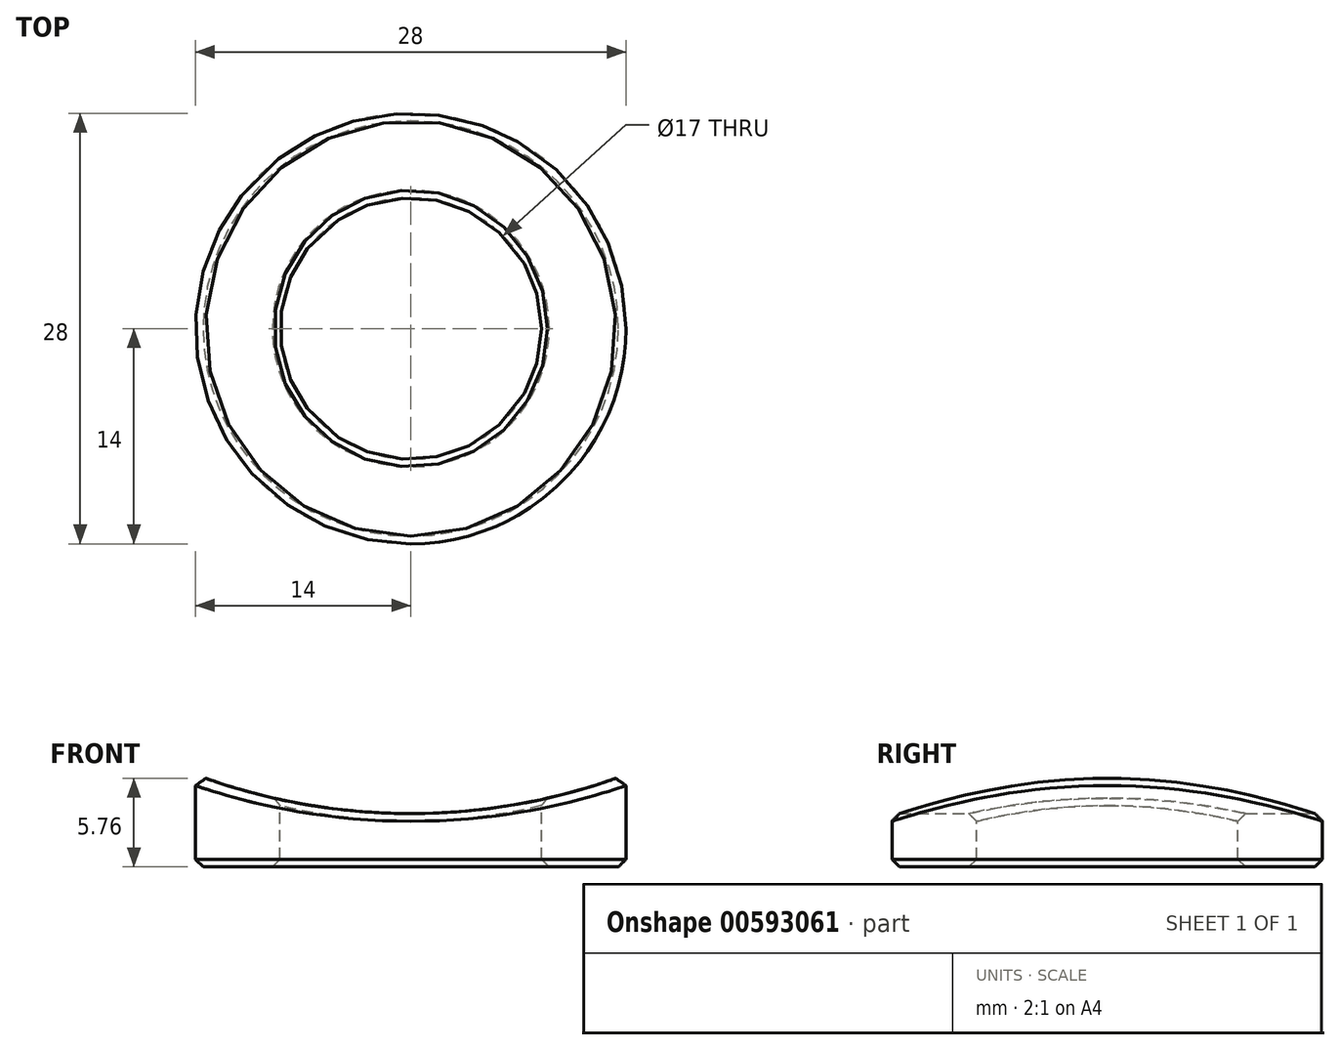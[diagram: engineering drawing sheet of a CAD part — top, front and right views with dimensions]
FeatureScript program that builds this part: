
annotation { "Feature Type Name" : "Feature", "Feature Type Description" : "" }
export const myFeature = defineFeature(function(context is Context, id is Id, definition is map)
    precondition{}
    {
        {
            var Q0;
            Q0=qCreatedBy(makeId("Front.planeOp"),FACE);
            var sketch = newSketch(context, id + "F0", { "sketchPlane" : qUnion([Q0])});
            skArc(sketch, "E0", {"start": v(-14, 6) * mm, "mid": v(0, 3.47) * mm, "end": v(14, 6) * mm});
            skLineSegment(sketch, "E1", {"start": v(-14, 0) * mm, "end": v(14, 0) * mm});
            skLineSegment(sketch, "E2", {"start": v(14, 0) * mm, "end": v(14, 6) * mm});
            skLineSegment(sketch, "E3", {"start": v(-14, 0) * mm, "end": v(-14, 6) * mm});
            skSolve(sketch);
        }
        {
            var Q0;
            Q0=makeQuery(id+"F0.imprint","IMPRINT",FACE,{"disambiguationData":[TD([[makeQuery(id+"F0.imprint","IMPRINT",EDGE,{"derivedFrom":sQuery(id+"F0.wireOp",EDGE,"E0")}),-1.0]])]});
            extrude(context, id + "F1", {"entities" : qUnion([Q0]), "endBound" : BoundingType.SYMMETRIC, "depth" : 28 * mm, "offsetDistance" : 25 * mm});
        }
        {
            var Q0;
            Q0=qCreatedBy(makeId("Top.planeOp"),FACE);
            var sketch = newSketch(context, id + "F2", { "sketchPlane" : qUnion([Q0])});
            skCircle(sketch, "E4", {"center": v(0, 0) * mm, "radius": 14 * mm});
            skLineSegment(sketch, "E5.bottom", {"start": v(-16.22, 16.1) * mm, "end": v(16.48, 16.1) * mm});
            skLineSegment(sketch, "E5.top", {"start": v(-16.22, -16.1) * mm, "end": v(16.48, -16.1) * mm});
            skLineSegment(sketch, "E5.left", {"start": v(-16.22, 16.1) * mm, "end": v(-16.22, -16.1) * mm});
            skLineSegment(sketch, "E5.right", {"start": v(16.48, 16.1) * mm, "end": v(16.48, -16.1) * mm});
            skSolve(sketch);
        }
        {
            var Q0;
            Q0 = qSketchRegion(id + "F2", true);
            extrude(context, id + "F3", {"entities" : qUnion([Q0]), "operationType" : NewBodyOperationType.REMOVE, "endBound" : BoundingType.SYMMETRIC, "oppositeDirection" : true, "depth" : 100 * mm, "offsetDistance" : 25 * mm});
        }
        {
            var Q0;
            Q0=qCreatedBy(makeId("Top.planeOp"),FACE);
            var sketch = newSketch(context, id + "F4", { "sketchPlane" : qUnion([Q0])});
            skCircle(sketch, "E6", {"center": v(0, 0) * mm, "radius": 8.5 * mm});
            skSolve(sketch);
        }
        {
            var Q0;
            Q0 = qSketchRegion(id + "F4", true);
            extrude(context, id + "F5", {"entities" : qUnion([Q0]), "operationType" : NewBodyOperationType.REMOVE, "endBound" : BoundingType.SYMMETRIC, "oppositeDirection" : true, "depth" : 100 * mm, "offsetDistance" : 25 * mm});
        }
        {
            var Q0;
            Q0=makeQuery(id+"F3.boolean.opBoolean","INTERSECT",EDGE,{"derivedFrom":[makeQuery(id+"F1.opExtrude","SWEPT_FACE",FACE,{"disambiguationData":[OSD([sQuery(id+"F0.wireOp",EDGE,"E0")])]}),makeQuery(id+"F3.opExtrude","SWEPT_FACE",FACE,{"disambiguationData":[OSD([sQuery(id+"F2.wireOp",EDGE,"E4")])]})]});
            var Q1;
            Q1=makeQuery(id+"F5.boolean.opBoolean","INTERSECT",EDGE,{"derivedFrom":[makeQuery(id+"F1.opExtrude","SWEPT_FACE",FACE,{"disambiguationData":[OSD([sQuery(id+"F0.wireOp",EDGE,"E0")])]}),makeQuery(id+"F5.opExtrude","SWEPT_FACE",FACE,{"disambiguationData":[OSD([sQuery(id+"F4.wireOp",EDGE,"E6")])]})]});
            var Q2;
            Q2=makeQuery(id+"F5.boolean.opBoolean","INTERSECT",EDGE,{"derivedFrom":[makeQuery(id+"F1.opExtrude","SWEPT_FACE",FACE,{"disambiguationData":[OSD([sQuery(id+"F0.wireOp",EDGE,"E1")])]}),makeQuery(id+"F5.opExtrude","SWEPT_FACE",FACE,{"disambiguationData":[OSD([sQuery(id+"F4.wireOp",EDGE,"E6")])]})]});
            var Q3;
            Q3=makeQuery(id+"F3.boolean.opBoolean","INTERSECT",EDGE,{"derivedFrom":[makeQuery(id+"F1.opExtrude","SWEPT_FACE",FACE,{"disambiguationData":[OSD([sQuery(id+"F0.wireOp",EDGE,"E1")])]}),makeQuery(id+"F3.opExtrude","SWEPT_FACE",FACE,{"disambiguationData":[OSD([sQuery(id+"F2.wireOp",EDGE,"E4")])]})]});
            chamfer(context, id + "F6", {"entities" : qUnion([Q0, Q1, Q2, Q3]), "width" : 0.5 * mm, "tangentPropagation" : true});
        }
    });
